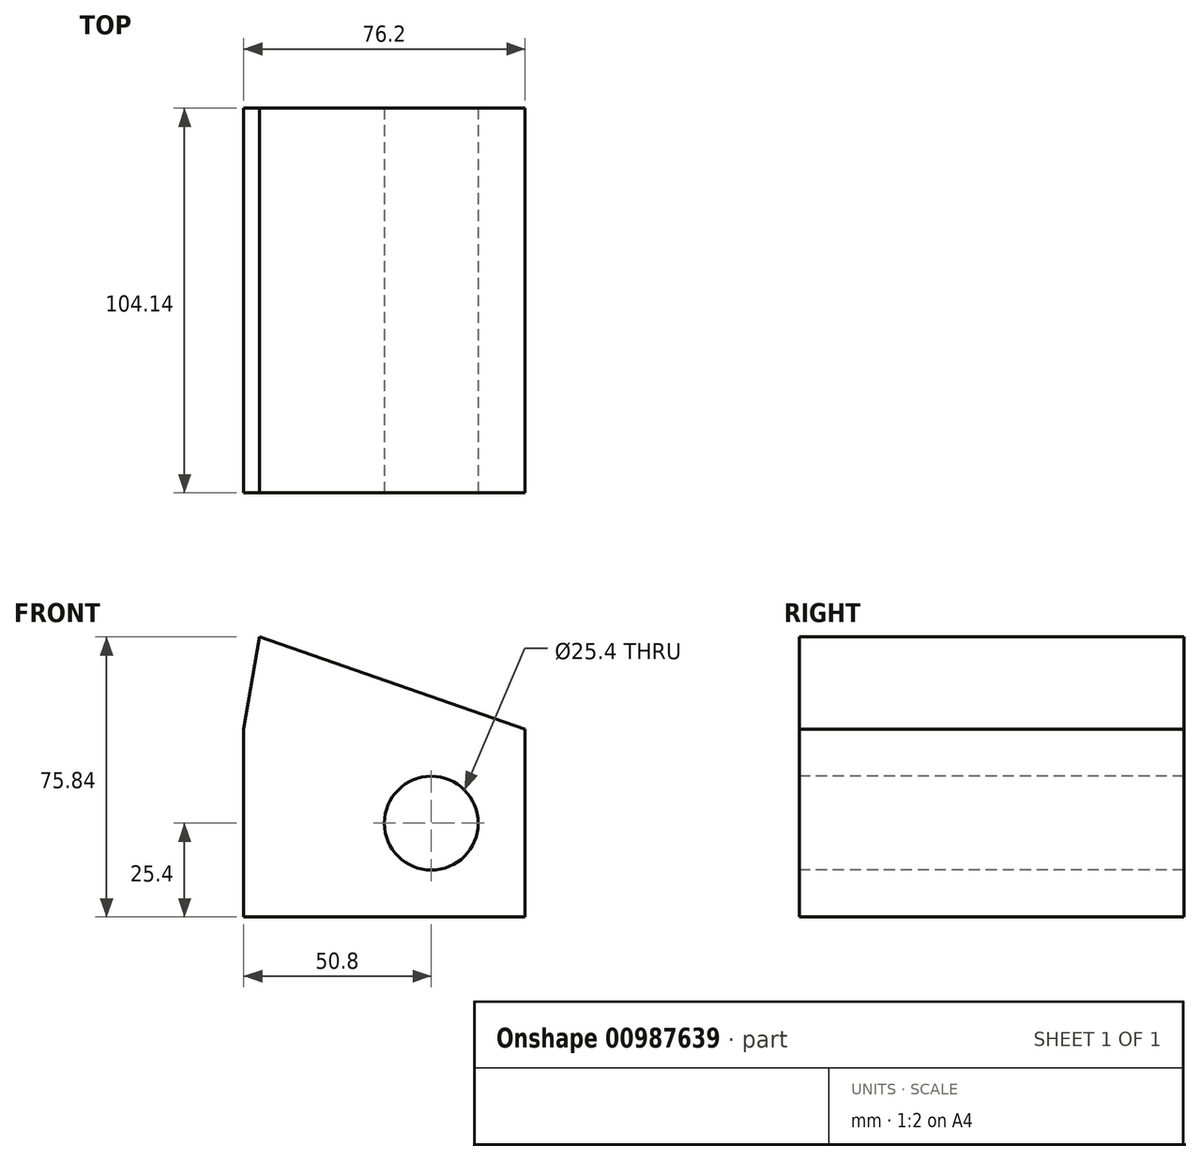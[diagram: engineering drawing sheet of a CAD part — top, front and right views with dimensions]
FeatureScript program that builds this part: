
annotation { "Feature Type Name" : "Feature", "Feature Type Description" : "" }
export const myFeature = defineFeature(function(context is Context, id is Id, definition is map)
    precondition{}
    {
        {
            var Q0;
            Q0=qCreatedBy(makeId("Front.planeOp"),FACE);
            var sketch = newSketch(context, id + "F0", { "sketchPlane" : qUnion([Q0])});
            skLineSegment(sketch, "E0.bottom", {"start": v(0, 0) * mm, "end": v(76.2, 0) * mm});
            skLineSegment(sketch, "E0.top", {"start": v(0, 50.8) * mm, "end": v(76.2, 50.8) * mm});
            skLineSegment(sketch, "E0.left", {"start": v(0, 0) * mm, "end": v(0, 50.8) * mm});
            skLineSegment(sketch, "E0.right", {"start": v(76.2, 0) * mm, "end": v(76.2, 50.8) * mm});
            skLineSegment(sketch, "E1", {"start": v(0, 50.8) * mm, "end": v(4.23, 75.84) * mm});
            skLineSegment(sketch, "E2", {"start": v(4.23, 75.84) * mm, "end": v(76.2, 50.8) * mm});
            skSolve(sketch);
        }
        {
            var Q0;
            Q0=makeQuery(id+"F0.imprint","IMPRINT",FACE,{"disambiguationData":[TD([[makeQuery(id+"F0.imprint","IMPRINT",EDGE,{"derivedFrom":sQuery(id+"F0.wireOp",EDGE,"E0.bottom")}),1.0]])]});
            var Q1;
            Q1=makeQuery(id+"F0.imprint","IMPRINT",FACE,{"disambiguationData":[TD([[makeQuery(id+"F0.imprint","IMPRINT",EDGE,{"derivedFrom":sQuery(id+"F0.wireOp",EDGE,"E0.top")}),1.0]])]});
            extrude(context, id + "F1", {"entities" : qUnion([Q0, Q1]), "depth" : 104.14 * mm, "offsetDistance" : 25.4 * mm});
        }
        {
            var Q0;
            Q0=makeQuery(id+"F1.opExtrude","CAP_FACE",FACE,{"disambiguationData":[OSD([sQuery(id+"F0.wireOp",EDGE,"E0.bottom"),sQuery(id+"F0.wireOp",EDGE,"E0.left"),sQuery(id+"F0.wireOp",EDGE,"E0.right"),sQuery(id+"F0.wireOp",EDGE,"E1"),sQuery(id+"F0.wireOp",EDGE,"E2")])],"isStart":false});
            var sketch = newSketch(context, id + "F2", { "sketchPlane" : qUnion([Q0])});
            skCircle(sketch, "E3", {"center": v(50.8, 25.4) * mm, "radius": 12.7 * mm});
            skSolve(sketch);
        }
        {
            var Q0;
            Q0 = qSketchRegion(id + "F2", true);
            extrude(context, id + "F3", {"entities" : qUnion([Q0]), "operationType" : NewBodyOperationType.REMOVE, "oppositeDirection" : true, "depth" : 104.14 * mm, "offsetDistance" : 25.4 * mm});
        }
    });
